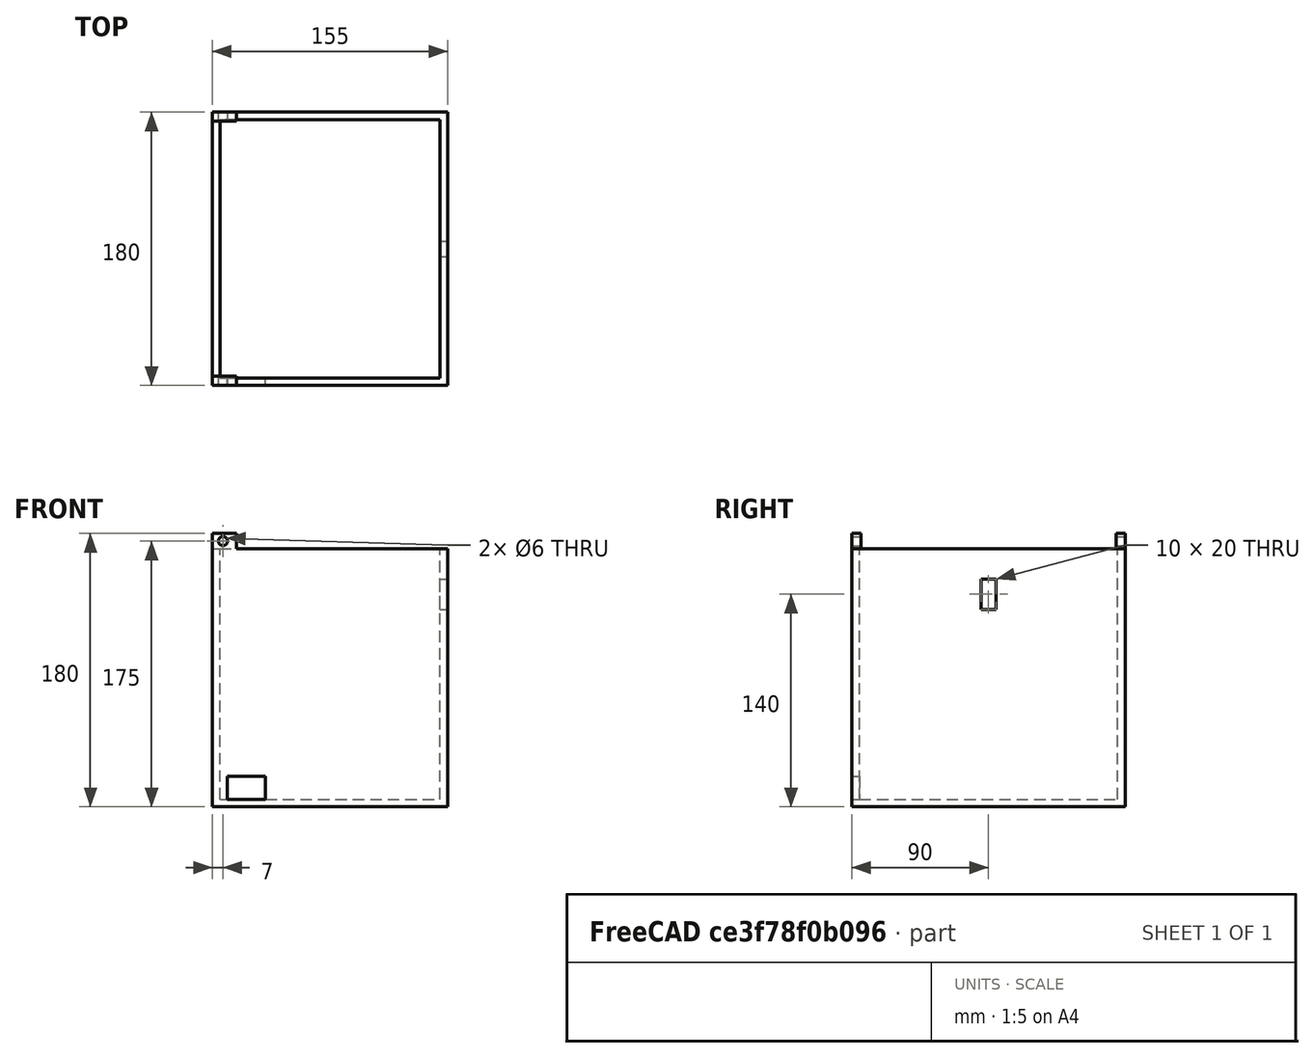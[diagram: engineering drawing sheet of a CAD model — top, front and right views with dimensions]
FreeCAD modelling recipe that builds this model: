
FCSTD DOCUMENT  (FreeCAD 1.0R38806 (Git))
Label: Caja_sola
License: All rights reserved
LicenseURL: https://en.wikipedia.org/wiki/All_rights_reserved
objects: Part::Box×6, Part::Cut×5, Part::Cylinder×2, Part::Fuse×2
note: 15 computed .brp shape members not serialized (recipe doc carries the construction recipe); baked Part::Feature solids carry a one-line shape summary decoded from their .brp

FEATURE [Part::Box] Box008  label="Cube004"
  AttacherType = Attacher::AttachEngine3D
  Height = 170
  Length = 155
  Width = 180
FEATURE [Part::Box] Box009  label="Cube005"
  AttacherType = Attacher::AttachEngine3D
  Height = 200
  Length = 145
  Placement = pos=(5,5,5) rot=(0,0,1;0rad)
  Width = 170
FEATURE [Part::Box] Box010  label="Agujero001"
  AttacherType = Attacher::AttachEngine3D
  Height = 15
  Length = 25
  Placement = pos=(10,-7,5) rot=(0,0,1;0rad)
  Width = 25
FEATURE [Part::Box] Box011  label="Cube006"
  AttacherType = Attacher::AttachEngine3D
  Height = 20
  Length = 12
  Placement = pos=(146,85,130) rot=(0,0,1;0rad)
  Width = 10
FEATURE [Part::Box] Box012  label="visagra_1_002"
  AttacherType = Attacher::AttachEngine3D
  Height = 10
  Length = 16
  Placement = pos=(0,174,170) rot=(0,0,1;0rad)
  Width = 6
FEATURE [Part::Box] Box013  label="visagra2_002"
  AttacherType = Attacher::AttachEngine3D
  Height = 10
  Length = 16
  Placement = pos=(0,0,170) rot=(0,0,1;0rad)
  Width = 6
FEATURE [Part::Cut] Cut006  label="EStructura001"
  Base = -> Box008
  Refine = true
  Tool = -> Box009
FEATURE [Part::Cut] Cut007  label="Caja_p002"
  Base = -> Cut006
  Refine = true
  Tool = -> Box010
FEATURE [Part::Cut] Cut008  label="Caja001"
  Base = -> Cut007
  Refine = true
  Tool = -> Box011
FEATURE [Part::Cylinder] Cylinder002
  Angle = 360
  AttacherType = Attacher::AttachEngine3D
  FirstAngle = 0
  Height = 148
  Placement = pos=(7,192,175) rot=(1,0,0;1.5708rad)
  Radius = 3
  SecondAngle = 0
FEATURE [Part::Cut] Cut009  label="visagra003"
  Base = -> Box012
  Refine = true
  Tool = -> Cylinder002
FEATURE [Part::Cylinder] Cylinder003
  Angle = 360
  AttacherType = Attacher::AttachEngine3D
  FirstAngle = 0
  Height = 148
  Placement = pos=(7,139,175) rot=(1,0,0;1.5708rad)
  Radius = 3
  SecondAngle = 0
FEATURE [Part::Cut] Cut010  label="visagra004"
  Base = -> Box013
  Refine = true
  Tool = -> Cylinder003
FEATURE [Part::Fuse] Fusion003
  Base = -> Cut008
  Refine = true
  Tool = -> Cut009
FEATURE [Part::Fuse] Fusion004  label="Caja002"
  Base = -> Fusion003
  Refine = true
  Tool = -> Cut010
